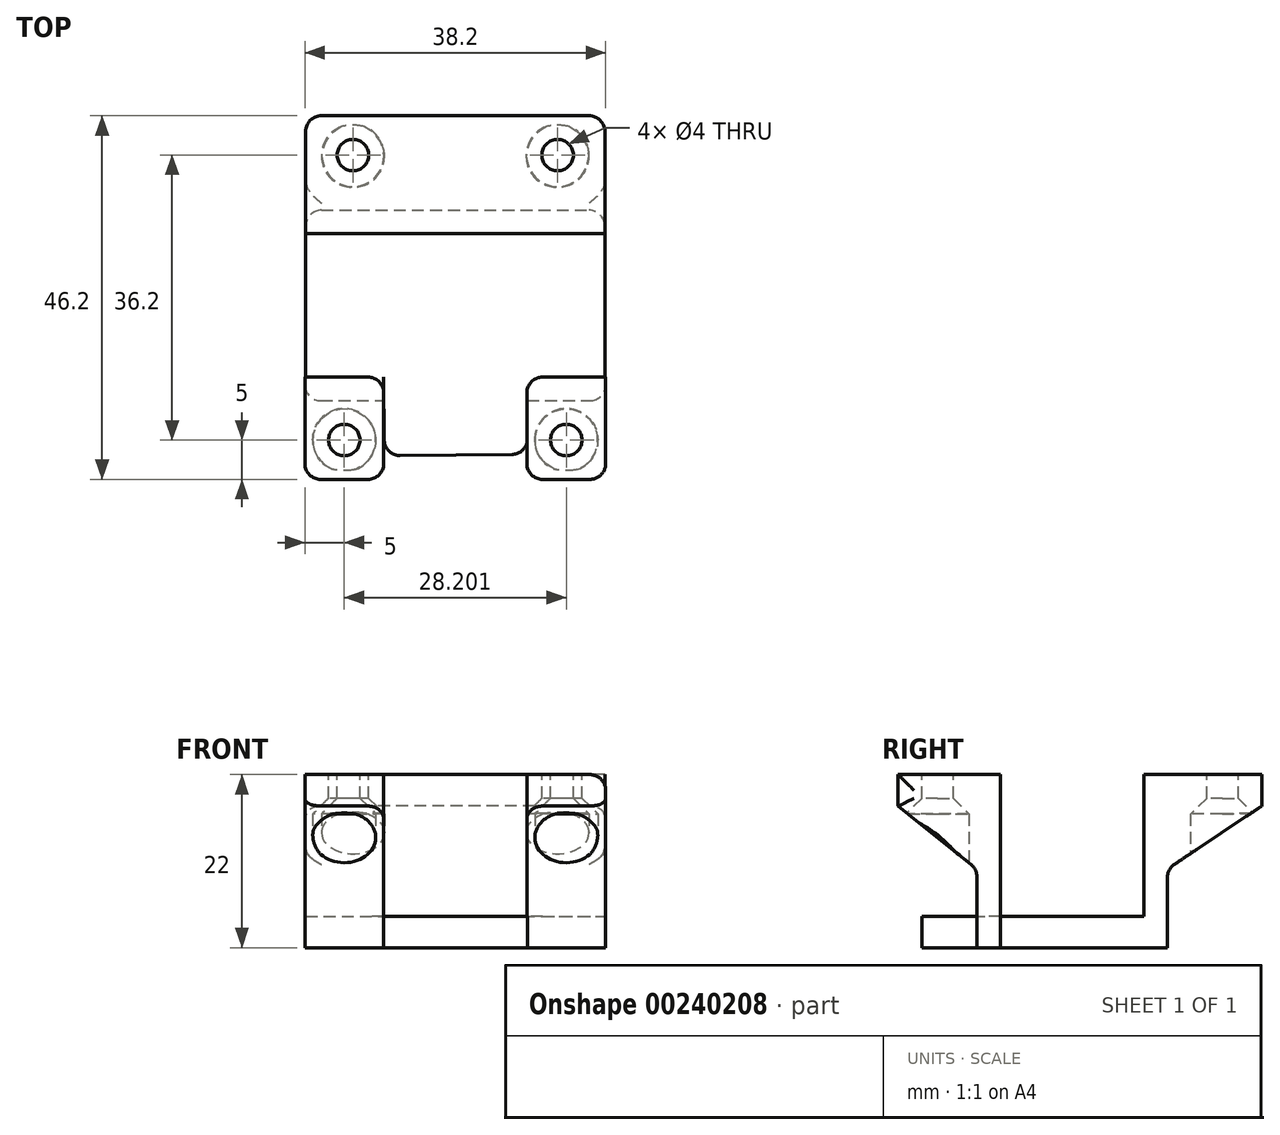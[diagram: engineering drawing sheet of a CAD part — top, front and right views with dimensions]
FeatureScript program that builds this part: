
annotation { "Feature Type Name" : "Feature", "Feature Type Description" : "" }
export const myFeature = defineFeature(function(context is Context, id is Id, definition is map)
    precondition{}
    {
        {
            var Q0;
            Q0=qCreatedBy(makeId("Top.planeOp"),FACE);
            var sketch = newSketch(context, id + "F0", { "sketchPlane" : qUnion([Q0])});
            skLineSegment(sketch, "E0.bottom", {"start": v(-19, 9.1) * mm, "end": v(19, 9.1) * mm});
            skLineSegment(sketch, "E0.top", {"start": v(-19, -9.1) * mm, "end": v(-9.1, -9.1) * mm});
            skLineSegment(sketch, "E0.left", {"start": v(-19, 9.1) * mm, "end": v(-19, -9.1) * mm});
            skLineSegment(sketch, "E0.right", {"start": v(19, 9.1) * mm, "end": v(19, -9.1) * mm});
            skPoint(sketch, "E0.middle", {"position": v(0, 0) * mm});
            skLineSegment(sketch, "E1.bottom", {"start": v(9.2, -18.92) * mm, "end": v(-9, -19.1) * mm});
            skLineSegment(sketch, "E1.left", {"start": v(9.2, -18.92) * mm, "end": v(9.1, -9.1) * mm});
            skLineSegment(sketch, "E1.right", {"start": v(-9, -19.1) * mm, "end": v(-9.1, -9.1) * mm});
            skPoint(sketch, "E1.middle", {"position": v(0, -9.1) * mm});
            skPoint(sketch, "E2.orphan", {"position": v(-9.2, 0.72) * mm});
            skPoint(sketch, "E3.orphan", {"position": v(9, 0.9) * mm});
            skLineSegment(sketch, "E4.trimOffspring", {"start": v(9.1, -9.1) * mm, "end": v(19, -9.1) * mm});
            skSolve(sketch);
        }
        {
            var Q0;
            Q0 = qSketchRegion(id + "F0", true);
            extrude(context, id + "F1", {"entities" : qUnion([Q0]), "depth" : 4 * mm});
        }
        {
            var Q0;
            Q0=qCreatedBy(makeId("Top.planeOp"),FACE);
            var sketch = newSketch(context, id + "F2", { "sketchPlane" : qUnion([Q0])});
            skLineSegment(sketch, "E5.bottom", {"start": v(-19.1, -9.1) * mm, "end": v(-9.1, -9.1) * mm});
            skLineSegment(sketch, "E5.top", {"start": v(-19.1, -12.1) * mm, "end": v(-9.1, -12.1) * mm});
            skLineSegment(sketch, "E5.left", {"start": v(-19.1, -9.1) * mm, "end": v(-19.1, -12.1) * mm});
            skLineSegment(sketch, "E5.right", {"start": v(-9.1, -9.1) * mm, "end": v(-9.1, -12.1) * mm});
            skLineSegment(sketch, "E6.bottom", {"start": v(9.1, -9.1) * mm, "end": v(19.1, -9.1) * mm});
            skLineSegment(sketch, "E6.top", {"start": v(9.1, -12.1) * mm, "end": v(19.1, -12.1) * mm});
            skLineSegment(sketch, "E6.left", {"start": v(9.1, -9.1) * mm, "end": v(9.1, -12.1) * mm});
            skLineSegment(sketch, "E6.right", {"start": v(19.1, -9.1) * mm, "end": v(19.1, -12.1) * mm});
            skLineSegment(sketch, "E7.bottom", {"start": v(-19, 12.1) * mm, "end": v(19, 12.1) * mm});
            skLineSegment(sketch, "E7.top", {"start": v(-19, 9.1) * mm, "end": v(19, 9.1) * mm});
            skLineSegment(sketch, "E7.left", {"start": v(-19, 12.1) * mm, "end": v(-19, 9.1) * mm});
            skLineSegment(sketch, "E7.right", {"start": v(19, 12.1) * mm, "end": v(19, 9.1) * mm});
            skSolve(sketch);
        }
        {
            var Q0;
            Q0 = qSketchRegion(id + "F2", true);
            extrude(context, id + "F3", {"entities" : qUnion([Q0]), "operationType" : NewBodyOperationType.ADD, "depth" : 22 * mm});
        }
        {
            var Q0;
            Q0=makeQuery(id+"F3.opExtrude","SWEPT_FACE",FACE,{"disambiguationData":[OSD([sQuery(id+"F2.wireOp",EDGE,"E5.top")])]});
            var sketch = newSketch(context, id + "F4", { "sketchPlane" : qUnion([Q0])});
            skLineSegment(sketch, "E8.bottom", {"start": v(-19.1, 22) * mm, "end": v(-9.1, 22) * mm});
            skLineSegment(sketch, "E8.top", {"start": v(-19.1, 10) * mm, "end": v(-9.1, 10) * mm});
            skLineSegment(sketch, "E8.left", {"start": v(-19.1, 22) * mm, "end": v(-19.1, 10) * mm});
            skLineSegment(sketch, "E8.right", {"start": v(-9.1, 22) * mm, "end": v(-9.1, 10) * mm});
            skLineSegment(sketch, "E9.bottom", {"start": v(9.1, 22) * mm, "end": v(19.1, 22) * mm});
            skLineSegment(sketch, "E9.top", {"start": v(9.1, 10) * mm, "end": v(19.1, 10) * mm});
            skLineSegment(sketch, "E9.left", {"start": v(9.1, 22) * mm, "end": v(9.1, 10) * mm});
            skLineSegment(sketch, "E9.right", {"start": v(19.1, 22) * mm, "end": v(19.1, 10) * mm});
            skSolve(sketch);
        }
        {
            var Q0;
            Q0 = qSketchRegion(id + "F4", true);
            extrude(context, id + "F5", {"entities" : qUnion([Q0]), "operationType" : NewBodyOperationType.ADD, "depth" : 10 * mm});
        }
        {
            var Q0;
            Q0=makeQuery(id+"F5.boolean.opBoolean","MERGE",FACE,{"derivedFrom":[makeQuery(id+"F3.opExtrude","CAP_FACE",FACE,{"disambiguationData":[OSD([sQuery(id+"F2.wireOp",EDGE,"E6.bottom"),sQuery(id+"F2.wireOp",EDGE,"E6.top"),sQuery(id+"F2.wireOp",EDGE,"E6.left"),sQuery(id+"F2.wireOp",EDGE,"E6.right")])],"isStart":false}),makeQuery(id+"F5.opExtrude","SWEPT_FACE",FACE,{"disambiguationData":[OSD([sQuery(id+"F4.wireOp",EDGE,"E9.bottom")])]})]});
            var sketch = newSketch(context, id + "F6", { "sketchPlane" : qUnion([Q0])});
            skCircle(sketch, "E10", {"center": v(14.1, -17.1) * mm, "radius": 2 * mm});
            skPoint(sketch, "E10.centerSnap0", {"position": v(14.1, -9.1) * mm});
            skCircle(sketch, "E11", {"center": v(-14.1, -17.1) * mm, "radius": 2 * mm});
            skSolve(sketch);
        }
        {
            var Q0;
            Q0 = qSketchRegion(id + "F6", true);
            var Q1;
            Q1=makeQuery(id+"F3.boolean.opBoolean","MERGE",FACE,{"derivedFrom":[makeQuery(id+"F1.opExtrude","CAP_FACE",FACE,{"disambiguationData":[OSD([sQuery(id+"F0.wireOp",EDGE,"E0.bottom"),sQuery(id+"F0.wireOp",EDGE,"E0.top"),sQuery(id+"F0.wireOp",EDGE,"E0.left"),sQuery(id+"F0.wireOp",EDGE,"E0.right"),sQuery(id+"F0.wireOp",EDGE,"E1.bottom"),sQuery(id+"F0.wireOp",EDGE,"E1.left"),sQuery(id+"F0.wireOp",EDGE,"E1.right"),sQuery(id+"F0.wireOp",EDGE,"E4.trimOffspring")])],"isStart":true}),makeQuery(id+"F3.opExtrude","CAP_FACE",FACE,{"disambiguationData":[OSD([sQuery(id+"F2.wireOp",EDGE,"E5.bottom"),sQuery(id+"F2.wireOp",EDGE,"E5.top"),sQuery(id+"F2.wireOp",EDGE,"E5.left"),sQuery(id+"F2.wireOp",EDGE,"E5.right")])],"isStart":true}),makeQuery(id+"F3.opExtrude","CAP_FACE",FACE,{"disambiguationData":[OSD([sQuery(id+"F2.wireOp",EDGE,"E6.bottom"),sQuery(id+"F2.wireOp",EDGE,"E6.top"),sQuery(id+"F2.wireOp",EDGE,"E6.left"),sQuery(id+"F2.wireOp",EDGE,"E6.right")])],"isStart":true}),makeQuery(id+"F3.opExtrude","CAP_FACE",FACE,{"disambiguationData":[OSD([sQuery(id+"F2.wireOp",EDGE,"E7.bottom"),sQuery(id+"F2.wireOp",EDGE,"E7.top"),sQuery(id+"F2.wireOp",EDGE,"E7.left"),sQuery(id+"F2.wireOp",EDGE,"E7.right")])],"isStart":true})]});
            extrude(context, id + "F7", {"entities" : qUnion([Q0]), "operationType" : NewBodyOperationType.REMOVE, "oppositeDirection" : true, "endBoundEntityFace" : qUnion([Q1]), "depth" : 12 * mm});
        }
        {
            var Q0;
            Q0=makeQuery(id+"F5.opExtrude","SWEPT_FACE",FACE,{"disambiguationData":[OSD([sQuery(id+"F4.wireOp",EDGE,"E8.top")])]});
            var sketch = newSketch(context, id + "F8", { "sketchPlane" : qUnion([Q0])});
            skCircle(sketch, "E12", {"center": v(-14.1, 17.1) * mm, "radius": 4 * mm});
            skCircle(sketch, "E13", {"center": v(14.1, 17.1) * mm, "radius": 4 * mm});
            skSolve(sketch);
        }
        {
            var Q0;
            Q0 = qSketchRegion(id + "F8", true);
            extrude(context, id + "F9", {"entities" : qUnion([Q0]), "operationType" : NewBodyOperationType.REMOVE, "oppositeDirection" : true, "depth" : 7 * mm});
        }
        {
            var Q0;
            Q0=makeQuery(id+"F3.opExtrude","SWEPT_FACE",FACE,{"disambiguationData":[OSD([sQuery(id+"F2.wireOp",EDGE,"E7.bottom")])]});
            var sketch = newSketch(context, id + "F10", { "sketchPlane" : qUnion([Q0])});
            skLineSegment(sketch, "E14.bottom", {"start": v(19, 22) * mm, "end": v(-19, 22) * mm});
            skLineSegment(sketch, "E14.top", {"start": v(19, 10) * mm, "end": v(-19, 10) * mm});
            skLineSegment(sketch, "E14.left", {"start": v(19, 22) * mm, "end": v(19, 10) * mm});
            skLineSegment(sketch, "E14.right", {"start": v(-19, 22) * mm, "end": v(-19, 10) * mm});
            skSolve(sketch);
        }
        {
            var Q0;
            Q0 = qSketchRegion(id + "F10", true);
            extrude(context, id + "F11", {"entities" : qUnion([Q0]), "operationType" : NewBodyOperationType.ADD, "depth" : 12 * mm});
        }
        {
            var Q0;
            Q0=makeQuery(id+"F5.opExtrude","CAP_EDGE",EDGE,{"disambiguationData":[OSD([sQuery(id+"F4.wireOp",EDGE,"E9.top")])],"isStart":false});
            var Q1;
            Q1=makeQuery(id+"F5.opExtrude","CAP_EDGE",EDGE,{"disambiguationData":[OSD([sQuery(id+"F4.wireOp",EDGE,"E8.top")])],"isStart":false});
            chamfer(context, id + "F12", {"entities" : qUnion([Q0, Q1]), "chamferType" : ChamferType.TWO_OFFSETS, "width1" : 8 * mm, "oppositeDirection" : false, "width2" : 10 * mm, "tangentPropagation" : true});
        }
        {
            var Q0;
            Q0=makeQuery(id+"F12.opChamfer","BLEND_EDGE",EDGE,{"blendedFrom":[makeQuery(id+"F5.opExtrude","CAP_EDGE",EDGE,{"disambiguationData":[OSD([sQuery(id+"F4.wireOp",EDGE,"E9.top")])],"isStart":false}),makeQuery(id+"F3.opExtrude","SWEPT_FACE",FACE,{"disambiguationData":[OSD([sQuery(id+"F2.wireOp",EDGE,"E6.top")])]})],"blendedInto":[makeQuery(id+"F3.opExtrude","SWEPT_FACE",FACE,{"disambiguationData":[OSD([sQuery(id+"F2.wireOp",EDGE,"E6.top")])]})]});
            var Q1;
            Q1=makeQuery(id+"F12.opChamfer","BLEND_EDGE",EDGE,{"blendedFrom":[makeQuery(id+"F5.opExtrude","CAP_EDGE",EDGE,{"disambiguationData":[OSD([sQuery(id+"F4.wireOp",EDGE,"E8.top")])],"isStart":false}),makeQuery(id+"F3.opExtrude","SWEPT_FACE",FACE,{"disambiguationData":[OSD([sQuery(id+"F2.wireOp",EDGE,"E5.top")])]})],"blendedInto":[makeQuery(id+"F3.opExtrude","SWEPT_FACE",FACE,{"disambiguationData":[OSD([sQuery(id+"F2.wireOp",EDGE,"E5.top")])]})]});
            fillet(context, id + "F13", {"entities" : qUnion([Q0, Q1]), "radius" : 2 * mm, "tangentPropagation" : true, "allowEdgeOverflow" : false});
        }
        {
            var Q0;
            Q0=makeQuery(id+"F11.boolean.opBoolean","MERGE",FACE,{"derivedFrom":[makeQuery(id+"F3.opExtrude","CAP_FACE",FACE,{"disambiguationData":[OSD([sQuery(id+"F2.wireOp",EDGE,"E7.bottom"),sQuery(id+"F2.wireOp",EDGE,"E7.top"),sQuery(id+"F2.wireOp",EDGE,"E7.left"),sQuery(id+"F2.wireOp",EDGE,"E7.right")])],"isStart":false}),makeQuery(id+"F11.opExtrude","SWEPT_FACE",FACE,{"disambiguationData":[OSD([sQuery(id+"F10.wireOp",EDGE,"E14.bottom")])]})]});
            var sketch = newSketch(context, id + "F14", { "sketchPlane" : qUnion([Q0])});
            skCircle(sketch, "E15", {"center": v(-13, 19.1) * mm, "radius": 2 * mm});
            skCircle(sketch, "E16", {"center": v(13, 19.1) * mm, "radius": 2 * mm});
            skSolve(sketch);
        }
        {
            var Q0;
            Q0 = qSketchRegion(id + "F14", true);
            extrude(context, id + "F15", {"entities" : qUnion([Q0]), "operationType" : NewBodyOperationType.REMOVE, "oppositeDirection" : true, "depth" : 10 * mm});
        }
        {
            var Q0;
            Q0=makeQuery(id+"F11.opExtrude","SWEPT_FACE",FACE,{"disambiguationData":[OSD([sQuery(id+"F10.wireOp",EDGE,"E14.top")])]});
            var sketch = newSketch(context, id + "F16", { "sketchPlane" : qUnion([Q0])});
            skCircle(sketch, "E17", {"center": v(-13, -19) * mm, "radius": 4 * mm});
            skCircle(sketch, "E18", {"center": v(13, -19) * mm, "radius": 4 * mm});
            skSolve(sketch);
        }
        {
            var Q0;
            Q0 = qSketchRegion(id + "F16", true);
            extrude(context, id + "F17", {"entities" : qUnion([Q0]), "operationType" : NewBodyOperationType.REMOVE, "oppositeDirection" : true, "depth" : 7 * mm});
        }
        {
            var Q0;
            Q0=makeQuery(id+"F11.opExtrude","CAP_EDGE",EDGE,{"disambiguationData":[OSD([sQuery(id+"F10.wireOp",EDGE,"E14.top")])],"isStart":false});
            chamfer(context, id + "F18", {"entities" : qUnion([Q0]), "chamferType" : ChamferType.TWO_OFFSETS, "width1" : 12 * mm, "oppositeDirection" : false, "width2" : 8 * mm, "tangentPropagation" : true});
        }
        {
            var Q0;
            Q0=makeQuery(id+"F3.opExtrude","SWEPT_EDGE",EDGE,{"disambiguationData":[OSD([sQuery(id+"F2.wireOp",EDGE,"E7.bottom"),sQuery(id+"F2.wireOp",EDGE,"E7.right")])]});
            var Q1;
            Q1=makeQuery(id+"F3.opExtrude","SWEPT_EDGE",EDGE,{"disambiguationData":[OSD([sQuery(id+"F2.wireOp",EDGE,"E7.bottom"),sQuery(id+"F2.wireOp",EDGE,"E7.left")])]});
            var Q2;
            Q2=makeQuery(id+"F1.opExtrude","SWEPT_EDGE",EDGE,{"disambiguationData":[OSD([sQuery(id+"F0.wireOp",EDGE,"E1.bottom"),sQuery(id+"F0.wireOp",EDGE,"E1.right")])]});
            var Q3;
            Q3=makeQuery(id+"F1.opExtrude","SWEPT_EDGE",EDGE,{"disambiguationData":[OSD([sQuery(id+"F0.wireOp",EDGE,"E1.bottom"),sQuery(id+"F0.wireOp",EDGE,"E1.left")])]});
            var Q4;
            Q4=makeQuery(id+"F3.opExtrude","SWEPT_EDGE",EDGE,{"disambiguationData":[OSD([sQuery(id+"F2.wireOp",EDGE,"E6.top"),sQuery(id+"F2.wireOp",EDGE,"E6.right")])]});
            var Q5;
            Q5=makeQuery(id+"F3.opExtrude","SWEPT_EDGE",EDGE,{"disambiguationData":[OSD([sQuery(id+"F2.wireOp",EDGE,"E5.top"),sQuery(id+"F2.wireOp",EDGE,"E5.left")])]});
            var Q6;
            Q6=makeQuery(id+"F5.opExtrude","CAP_EDGE",EDGE,{"disambiguationData":[OSD([sQuery(id+"F4.wireOp",EDGE,"E9.left")])],"isStart":false});
            var Q7;
            Q7=makeQuery(id+"F5.boolean.opBoolean","MERGE",EDGE,{"derivedFrom":[makeQuery(id+"F3.opExtrude","CAP_EDGE",EDGE,{"disambiguationData":[OSD([sQuery(id+"F2.wireOp",EDGE,"E6.right")])],"isStart":false}),makeQuery(id+"F5.opExtrude","SWEPT_EDGE",EDGE,{"disambiguationData":[OSD([sQuery(id+"F4.wireOp",EDGE,"E9.bottom"),sQuery(id+"F4.wireOp",EDGE,"E9.right")])]})]});
            var Q8;
            Q8=makeQuery(id+"F5.opExtrude","CAP_EDGE",EDGE,{"disambiguationData":[OSD([sQuery(id+"F4.wireOp",EDGE,"E8.right")])],"isStart":false});
            var Q9;
            Q9=makeQuery(id+"F5.opExtrude","CAP_EDGE",EDGE,{"disambiguationData":[OSD([sQuery(id+"F4.wireOp",EDGE,"E8.left")])],"isStart":false});
            var Q10;
            Q10=makeQuery(id+"F11.opExtrude","CAP_EDGE",EDGE,{"disambiguationData":[OSD([sQuery(id+"F10.wireOp",EDGE,"E14.left")])],"isStart":false});
            var Q11;
            Q11=makeQuery(id+"F11.opExtrude","CAP_EDGE",EDGE,{"disambiguationData":[OSD([sQuery(id+"F10.wireOp",EDGE,"E14.right")])],"isStart":false});
            var Q12;
            Q12=makeQuery(id+"F18.opChamfer","BLEND_EDGE",EDGE,{"blendedFrom":[makeQuery(id+"F11.opExtrude","CAP_EDGE",EDGE,{"disambiguationData":[OSD([sQuery(id+"F10.wireOp",EDGE,"E14.top")])],"isStart":false}),makeQuery(id+"F3.opExtrude","SWEPT_FACE",FACE,{"disambiguationData":[OSD([sQuery(id+"F2.wireOp",EDGE,"E7.bottom")])]})],"blendedInto":[makeQuery(id+"F3.opExtrude","SWEPT_FACE",FACE,{"disambiguationData":[OSD([sQuery(id+"F2.wireOp",EDGE,"E7.bottom")])]})]});
            var Q13;
            Q13=makeQuery(id+"F5.opExtrude","CAP_EDGE",EDGE,{"disambiguationData":[OSD([sQuery(id+"F4.wireOp",EDGE,"E9.right")])],"isStart":false});
            fillet(context, id + "F19", {"entities" : qUnion([Q0, Q1, Q2, Q3, Q4, Q5, Q6, Q7, Q8, Q9, Q10, Q11, Q12, Q13]), "radius" : 2 * mm, "tangentPropagation" : true, "allowEdgeOverflow" : false});
        }
        {
            var Q0;
            Q0=makeQuery(id+"F9.boolean.opBoolean","INTERSECT",EDGE,{"derivedFrom":[makeQuery(id+"F7.boolean.opBoolean","COPY",FACE,{"derivedFrom":makeQuery(id+"F7.opExtrude","SWEPT_FACE",FACE,{"disambiguationData":[OSD([sQuery(id+"F6.wireOp",EDGE,"E10")])]})}),makeQuery(id+"F9.opExtrude","CAP_FACE",FACE,{"disambiguationData":[OSD([sQuery(id+"F8.wireOp",EDGE,"E13")])],"isStart":false})]});
            var Q1;
            Q1=makeQuery(id+"F9.boolean.opBoolean","INTERSECT",EDGE,{"derivedFrom":[makeQuery(id+"F7.boolean.opBoolean","COPY",FACE,{"derivedFrom":makeQuery(id+"F7.opExtrude","SWEPT_FACE",FACE,{"disambiguationData":[OSD([sQuery(id+"F6.wireOp",EDGE,"E11")])]})}),makeQuery(id+"F9.opExtrude","CAP_FACE",FACE,{"disambiguationData":[OSD([sQuery(id+"F8.wireOp",EDGE,"E12")])],"isStart":false})]});
            var Q2;
            Q2=makeQuery(id+"F17.boolean.opBoolean","INTERSECT",EDGE,{"derivedFrom":[makeQuery(id+"F15.boolean.opBoolean","COPY",FACE,{"derivedFrom":makeQuery(id+"F15.opExtrude","SWEPT_FACE",FACE,{"disambiguationData":[OSD([sQuery(id+"F14.wireOp",EDGE,"E15")])]})}),makeQuery(id+"F17.opExtrude","CAP_FACE",FACE,{"disambiguationData":[OSD([sQuery(id+"F16.wireOp",EDGE,"E17")])],"isStart":false})]});
            var Q3;
            Q3=makeQuery(id+"F17.boolean.opBoolean","INTERSECT",EDGE,{"derivedFrom":[makeQuery(id+"F15.boolean.opBoolean","COPY",FACE,{"derivedFrom":makeQuery(id+"F15.opExtrude","SWEPT_FACE",FACE,{"disambiguationData":[OSD([sQuery(id+"F14.wireOp",EDGE,"E16")])]})}),makeQuery(id+"F17.opExtrude","CAP_FACE",FACE,{"disambiguationData":[OSD([sQuery(id+"F16.wireOp",EDGE,"E18")])],"isStart":false})]});
            chamfer(context, id + "F20", {"entities" : qUnion([Q0, Q1, Q2, Q3]), "width" : 2 * mm, "tangentPropagation" : true});
        }
        {
            var Q0;
            Q0=makeQuery(id+"F3.boolean.opBoolean","SPLIT",EDGE,{"derivedFrom":makeQuery(id+"F3.opExtrude","SWEPT_EDGE",EDGE,{"disambiguationData":[OSD([sQuery(id+"F2.wireOp",EDGE,"E5.bottom"),sQuery(id+"F2.wireOp",EDGE,"E5.right")])]})});
            var Q1;
            Q1=makeQuery(id+"F3.opExtrude","SWEPT_EDGE",EDGE,{"disambiguationData":[OSD([sQuery(id+"F2.wireOp",EDGE,"E6.bottom"),sQuery(id+"F2.wireOp",EDGE,"E6.left")])]});
            fillet(context, id + "F21", {"entities" : qUnion([Q0, Q1]), "radius" : 2 * mm, "tangentPropagation" : true, "allowEdgeOverflow" : false});
        }
    });
